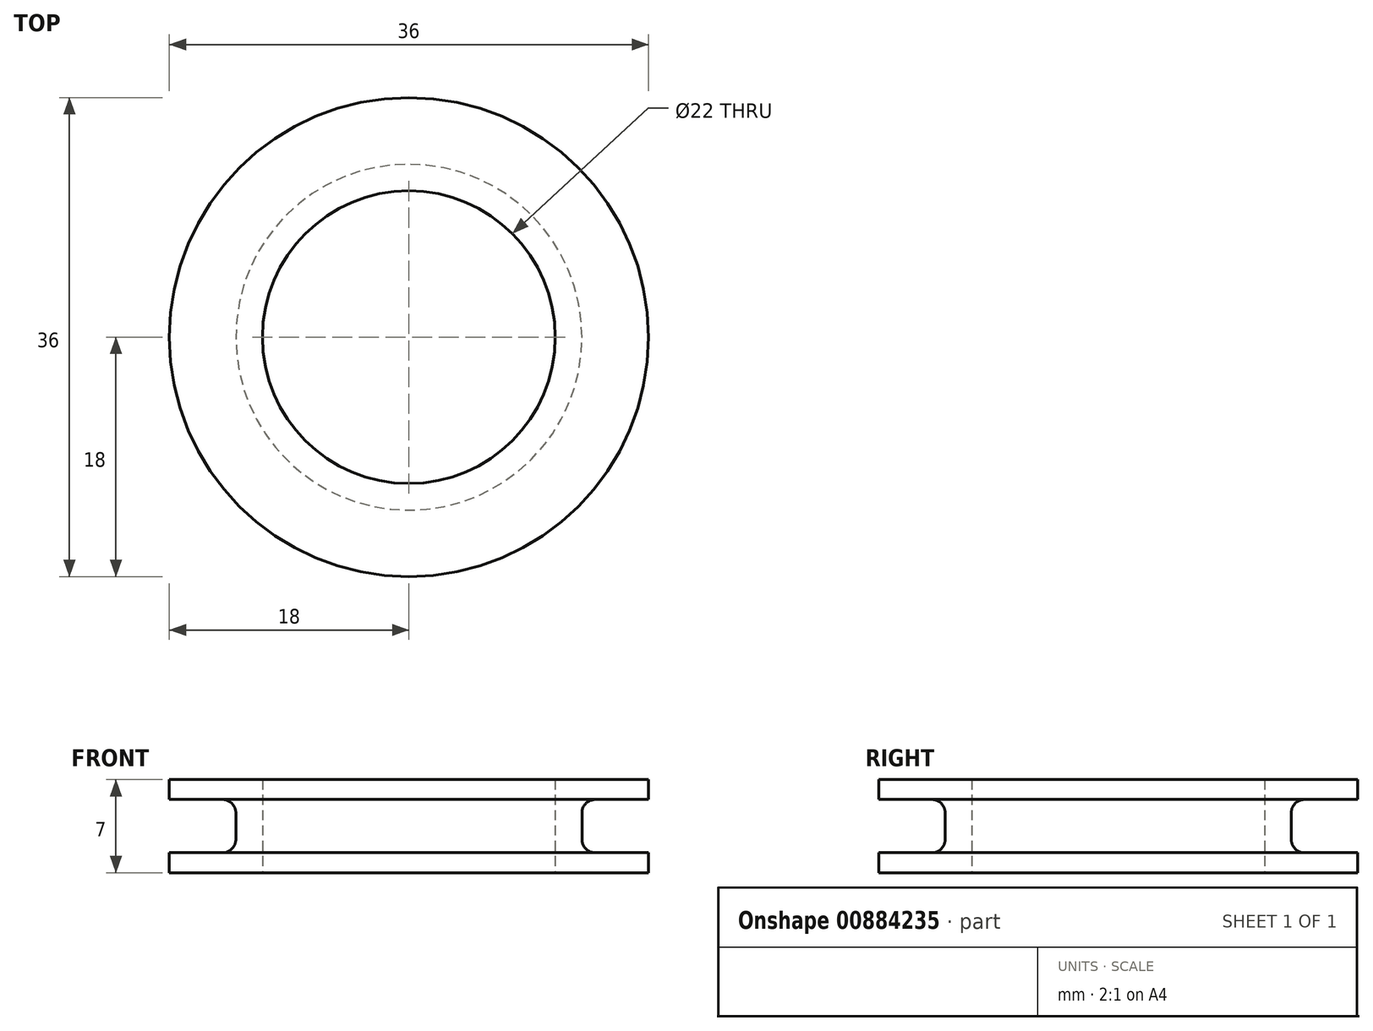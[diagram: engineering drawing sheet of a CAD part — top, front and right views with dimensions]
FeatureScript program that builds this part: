
annotation { "Feature Type Name" : "Feature", "Feature Type Description" : "" }
export const myFeature = defineFeature(function(context is Context, id is Id, definition is map)
    precondition{}
    {
        {
            var Q0;
            Q0=qCreatedBy(makeId("Front.planeOp"),FACE);
            var sketch = newSketch(context, id + "F0", { "sketchPlane" : qUnion([Q0])});
            skLineSegment(sketch, "E0", {"start": v(0, 0) * mm, "end": v(0, 3.5) * mm, "construction": true});
            skLineSegment(sketch, "E1", {"start": v(0, 3.5) * mm, "end": v(11, 3.5) * mm, "construction": true});
            skLineSegment(sketch, "E2", {"start": v(11, 3.5) * mm, "end": v(11, 0) * mm});
            skLineSegment(sketch, "E3", {"start": v(11, 3.5) * mm, "end": v(18, 3.5) * mm});
            skLineSegment(sketch, "E4.MirrorCS", {"start": v(11, -3.5) * mm, "end": v(11, 0) * mm});
            skLineSegment(sketch, "E5.MirrorCS", {"start": v(11, -3.5) * mm, "end": v(18, -3.5) * mm});
            skLineSegment(sketch, "E6", {"start": v(18, 3.5) * mm, "end": v(18, 2) * mm});
            skLineSegment(sketch, "E7", {"start": v(18, 2) * mm, "end": v(13, 2) * mm});
            skLineSegment(sketch, "E8", {"start": v(13, 2) * mm, "end": v(13, 0) * mm});
            skLineSegment(sketch, "E9.MirrorCS", {"start": v(13, -2) * mm, "end": v(13, 0) * mm});
            skLineSegment(sketch, "E10.MirrorCS", {"start": v(18, -2) * mm, "end": v(13, -2) * mm});
            skLineSegment(sketch, "E11.MirrorCS", {"start": v(18, -3.5) * mm, "end": v(18, -2) * mm});
            skSolve(sketch);
        }
        {
            var Q0;
            Q0=makeQuery(id+"F0.imprint","IMPRINT",FACE,{"disambiguationData":[TD([[makeQuery(id+"F0.imprint","IMPRINT",EDGE,{"derivedFrom":sQuery(id+"F0.wireOp",EDGE,"E2")}),1.0]])]});
            var Q1;
            Q1=sQuery(id+"F0.wireOp",EDGE,"E0");
            revolve(context, id + "F1", {"surfaceOperationType" : NewSurfaceOperationType.NEW, "entities" : qUnion([Q0]), "axis" : qUnion([Q1]), "revolveType" : RevolveType.FULL});
        }
        {
            var Q0;
            Q0=makeQuery(id+"F1.opRevolve","SWEPT_FACE",FACE,{"disambiguationData":[OSD([sQuery(id+"F0.wireOp",EDGE,"E8"),sQuery(id+"F0.wireOp",EDGE,"E9.MirrorCS")])]});
            fillet(context, id + "F2", {"entities" : qUnion([Q0]), "radius" : 1 * mm, "tangentPropagation" : true, "allowEdgeOverflow" : false});
        }
    });
